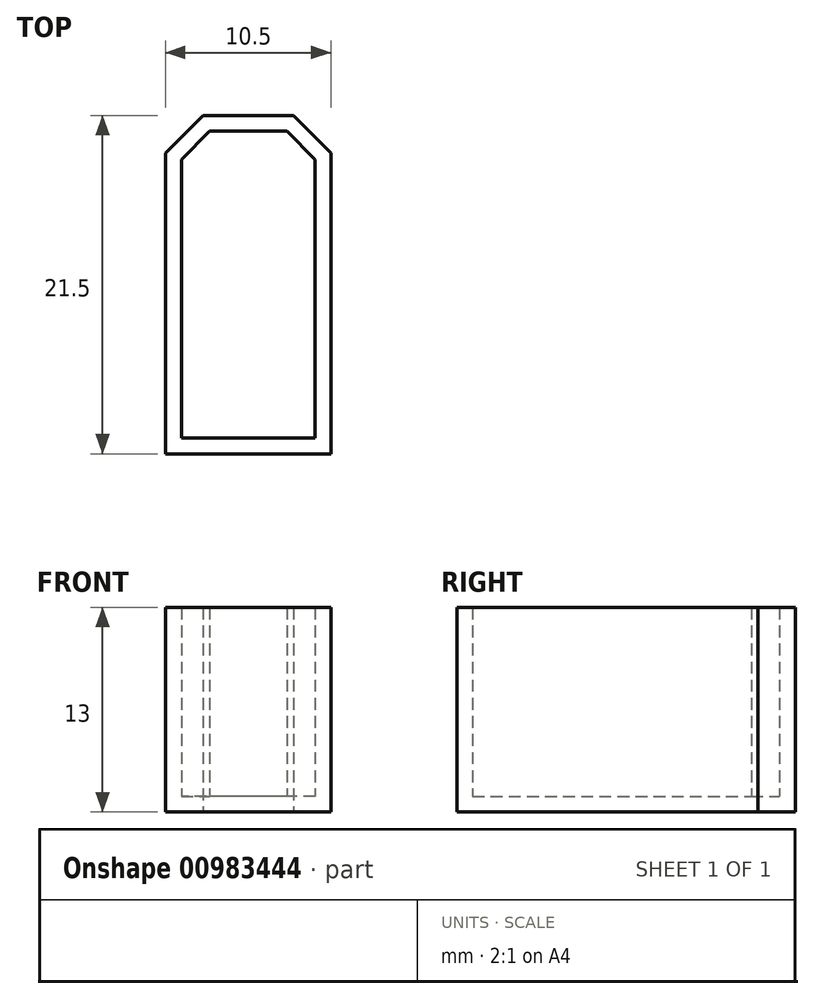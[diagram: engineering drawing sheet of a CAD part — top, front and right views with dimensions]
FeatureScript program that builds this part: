
annotation { "Feature Type Name" : "Feature", "Feature Type Description" : "" }
export const myFeature = defineFeature(function(context is Context, id is Id, definition is map)
    precondition{}
    {
        {
            var Q0;
            Q0=qCreatedBy(makeId("Top.planeOp"),FACE);
            var sketch = newSketch(context, id + "F0", { "sketchPlane" : qUnion([Q0])});
            skLineSegment(sketch, "E0.bottom", {"start": v(-2.45, 9.75) * mm, "end": v(2.45, 9.75) * mm});
            skLineSegment(sketch, "E0.top", {"start": v(-4.25, -9.75) * mm, "end": v(4.25, -9.75) * mm});
            skLineSegment(sketch, "E0.left", {"start": v(-4.25, 7.95) * mm, "end": v(-4.25, -9.75) * mm});
            skLineSegment(sketch, "E0.right", {"start": v(4.25, 7.95) * mm, "end": v(4.25, -9.75) * mm});
            skLineSegment(sketch, "E1", {"start": v(0, 9.75) * mm, "end": v(0, -9.75) * mm, "construction": true});
            skPoint(sketch, "E2", {"position": v(0, 0) * mm});
            skLineSegment(sketch, "E3", {"start": v(-2.45, 9.75) * mm, "end": v(-4.25, 7.95) * mm});
            skLineSegment(sketch, "E4.MirrorCS", {"start": v(2.45, 9.75) * mm, "end": v(4.25, 7.95) * mm});
            skPoint(sketch, "E5.orphan", {"position": v(-4.25, 9.75) * mm});
            skPoint(sketch, "E6.orphan", {"position": v(4.25, 9.75) * mm});
            skLineSegment(sketch, "E7.0", {"start": v(-2.86, 10.75) * mm, "end": v(-5.25, 8.36) * mm});
            skLineSegment(sketch, "E7.1", {"start": v(-5.25, -10.75) * mm, "end": v(5.25, -10.75) * mm});
            skLineSegment(sketch, "E7.2", {"start": v(5.25, 8.36) * mm, "end": v(5.25, -10.75) * mm});
            skLineSegment(sketch, "E7.3", {"start": v(-5.25, 8.36) * mm, "end": v(-5.25, -10.75) * mm});
            skLineSegment(sketch, "E7.4", {"start": v(2.86, 10.75) * mm, "end": v(5.25, 8.36) * mm});
            skLineSegment(sketch, "E7.5", {"start": v(-2.86, 10.75) * mm, "end": v(2.86, 10.75) * mm});
            skSolve(sketch);
        }
        {
            var Q0;
            Q0 = qSketchRegion(id + "F0", true);
            var Q1;
            Q1=makeQuery(id+"F0.imprint","IMPRINT",FACE,{"disambiguationData":[TD([[makeQuery(id+"F0.imprint","IMPRINT",EDGE,{"derivedFrom":sQuery(id+"F0.wireOp",EDGE,"E0.bottom")}),-1.0]])]});
            extrude(context, id + "F1", {"entities" : qUnion([Q0, Q1]), "depth" : 1 * mm, "offsetDistance" : 25.4 * mm});
        }
        {
            var Q0;
            Q0=makeQuery(id+"F0.imprint","IMPRINT",FACE,{"disambiguationData":[TD([[makeQuery(id+"F0.imprint","IMPRINT",EDGE,{"derivedFrom":sQuery(id+"F0.wireOp",EDGE,"E0.bottom")}),1.0]])]});
            extrude(context, id + "F2", {"entities" : qUnion([Q0]), "operationType" : NewBodyOperationType.ADD, "depth" : 13 * mm, "offsetDistance" : 25.4 * mm});
        }
    });
